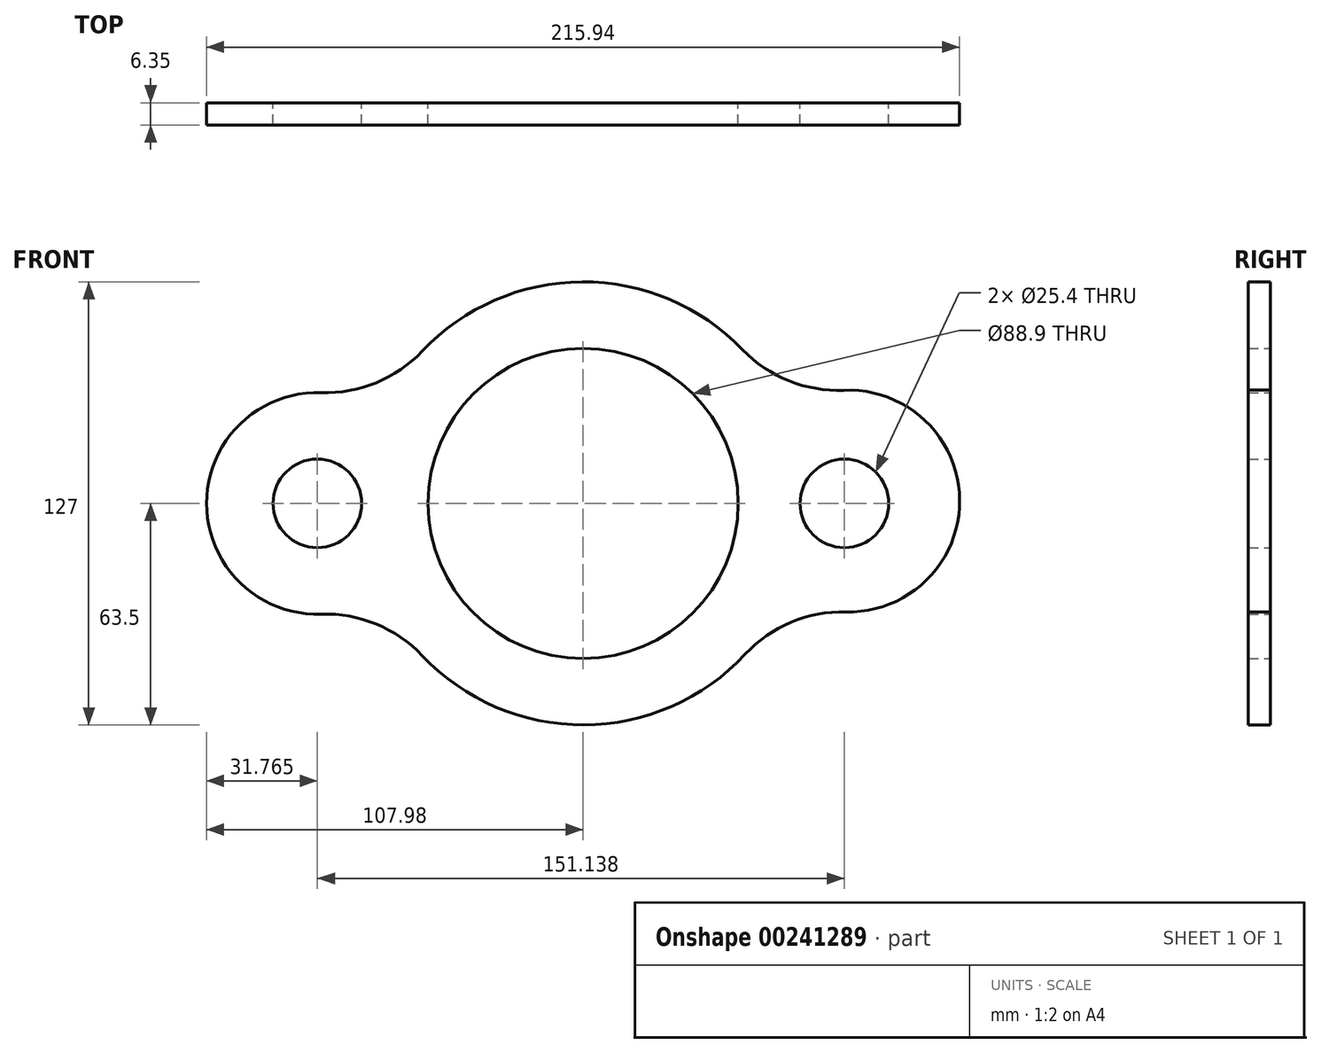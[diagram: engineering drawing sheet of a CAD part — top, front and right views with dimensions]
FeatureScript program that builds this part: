
annotation { "Feature Type Name" : "Feature", "Feature Type Description" : "" }
export const myFeature = defineFeature(function(context is Context, id is Id, definition is map)
    precondition{}
    {
        {
            var Q0;
            Q0=qCreatedBy(makeId("Front.planeOp"),FACE);
            var sketch = newSketch(context, id + "F0", { "sketchPlane" : qUnion([Q0])});
            skCircle(sketch, "E0", {"center": v(0, 0) * mm, "radius": 44.45 * mm});
            skCircle(sketch, "E1", {"center": v(-76.21, 0) * mm, "radius": 12.7 * mm});
            skCircle(sketch, "E2", {"center": v(74.92, 0) * mm, "radius": 12.7 * mm});
            skArc(sketch, "E3", {"start": v(-75.13, 31.74) * mm, "mid": v(-107.98, 0) * mm, "end": v(-75.13, -31.74) * mm});
            skArc(sketch, "E4.trimOffspring", {"start": v(-46.15, -43.64) * mm, "mid": v(0.26, -63.5) * mm, "end": v(46.5, -43.23) * mm});
            skArc(sketch, "E5.trimOffspring", {"start": v(45.71, 44.06) * mm, "mid": v(-0.3, 63.5) * mm, "end": v(-46.14, 43.64) * mm});
            skArc(sketch, "E6.trimOffspring", {"start": v(75.37, -31.09) * mm, "mid": v(107.96, 0.97) * mm, "end": v(74.8, 32.43) * mm});
            skPoint(sketch, "E7.visualSharp", {"position": v(-57.95, 25.99) * mm});
            skArc(sketch, "E7.filletArc", {"start": v(-75.13, 31.74) * mm, "mid": v(-59.36, 34.57) * mm, "end": v(-46.14, 43.64) * mm});
            skPoint(sketch, "E8.visualSharp", {"position": v(57.68, 26.52) * mm});
            skArc(sketch, "E8.filletArc", {"start": v(45.71, 44.06) * mm, "mid": v(59, 35.12) * mm, "end": v(74.8, 32.43) * mm});
            skPoint(sketch, "E9.visualSharp", {"position": v(58.15, -25.48) * mm});
            skArc(sketch, "E9.filletArc", {"start": v(75.37, -31.09) * mm, "mid": v(59.63, -34.05) * mm, "end": v(46.5, -43.23) * mm});
            skPoint(sketch, "E10.visualSharp", {"position": v(-57.95, -25.99) * mm});
            skArc(sketch, "E10.filletArc", {"start": v(-46.15, -43.64) * mm, "mid": v(-59.36, -34.57) * mm, "end": v(-75.13, -31.74) * mm});
            skSolve(sketch);
        }
        {
            var Q0;
            Q0 = qSketchRegion(id + "F0", true);
            extrude(context, id + "F1", {"entities" : qUnion([Q0]), "depth" : 6.35 * mm});
        }
    });
